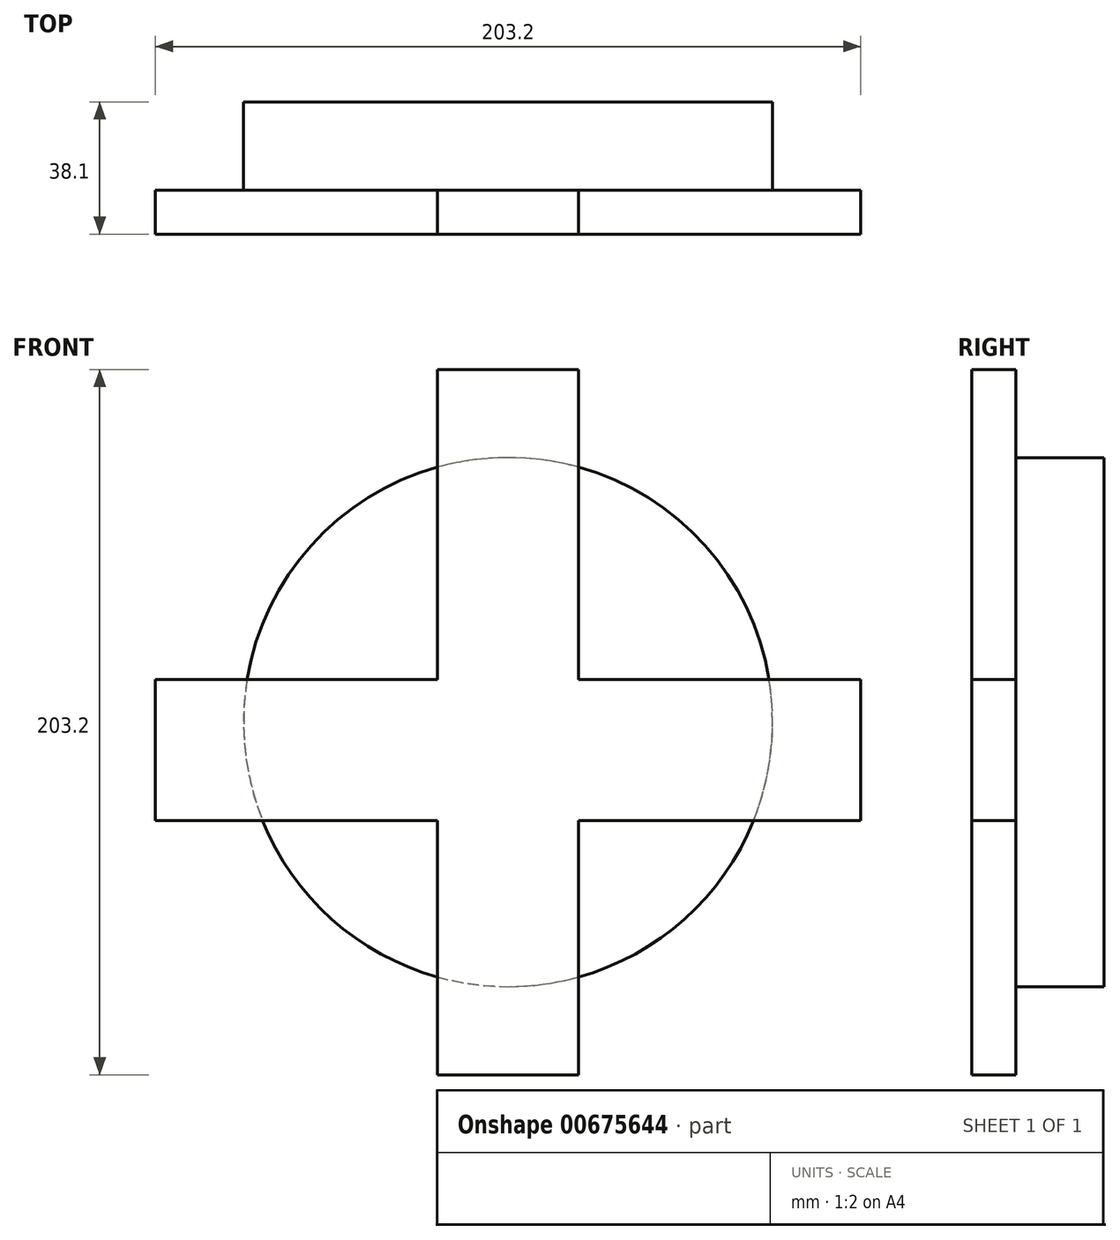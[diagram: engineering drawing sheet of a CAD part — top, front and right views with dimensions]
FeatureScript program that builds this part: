
annotation { "Feature Type Name" : "Feature", "Feature Type Description" : "" }
export const myFeature = defineFeature(function(context is Context, id is Id, definition is map)
    precondition{}
    {
        {
            var Q0;
            Q0=qCreatedBy(makeId("Front.planeOp"),FACE);
            var sketch = newSketch(context, id + "F0", { "sketchPlane" : qUnion([Q0])});
            skCircle(sketch, "E0", {"center": v(0, 0) * mm, "radius": 76.2 * mm});
            skSolve(sketch);
        }
        {
            var Q0;
            Q0 = qSketchRegion(id + "F0", true);
            extrude(context, id + "F1", {"entities" : qUnion([Q0]), "depth" : 25.4 * mm, "offsetDistance" : 25.4 * mm});
        }
        {
            var Q0;
            Q0=makeQuery(id+"F1.opExtrude","CAP_FACE",FACE,{"disambiguationData":[OSD([sQuery(id+"F0.wireOp",EDGE,"E0")])],"isStart":false});
            var sketch = newSketch(context, id + "F2", { "sketchPlane" : qUnion([Q0])});
            skLineSegment(sketch, "E1.bottom", {"start": v(-20.32, 101.6) * mm, "end": v(20.32, 101.6) * mm});
            skLineSegment(sketch, "E1.top", {"start": v(-20.32, -101.6) * mm, "end": v(20.32, -101.6) * mm});
            skLineSegment(sketch, "E1.left", {"start": v(-20.32, 101.6) * mm, "end": v(-20.32, -101.6) * mm});
            skLineSegment(sketch, "E1.right", {"start": v(20.32, 101.6) * mm, "end": v(20.32, -101.6) * mm});
            skLineSegment(sketch, "E2.bottom", {"start": v(-101.6, 12.32) * mm, "end": v(101.6, 12.32) * mm});
            skLineSegment(sketch, "E2.top", {"start": v(-101.6, -28.32) * mm, "end": v(101.6, -28.32) * mm});
            skLineSegment(sketch, "E2.left", {"start": v(-101.6, 12.32) * mm, "end": v(-101.6, -28.32) * mm});
            skLineSegment(sketch, "E2.right", {"start": v(101.6, 12.32) * mm, "end": v(101.6, -28.32) * mm});
            skSolve(sketch);
        }
        {
            var Q0;
            Q0 = qSketchRegion(id + "F2", true);
            extrude(context, id + "F3", {"entities" : qUnion([Q0]), "operationType" : NewBodyOperationType.ADD, "depth" : 12.7 * mm, "offsetDistance" : 25.4 * mm});
        }
    });
